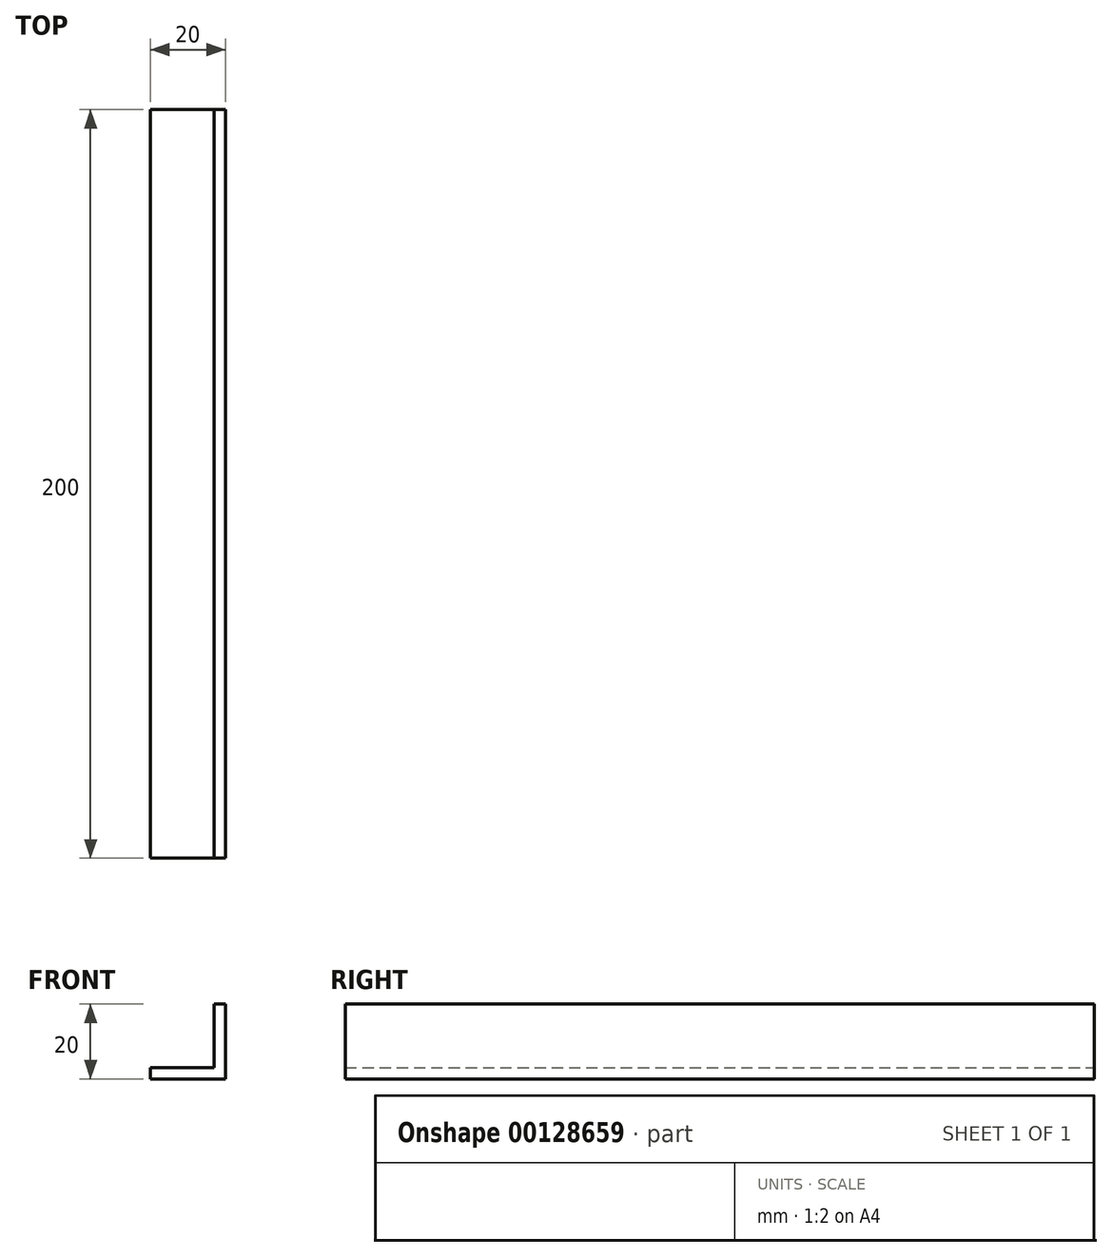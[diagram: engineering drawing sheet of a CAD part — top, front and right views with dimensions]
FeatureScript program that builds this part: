
annotation { "Feature Type Name" : "Feature", "Feature Type Description" : "" }
export const myFeature = defineFeature(function(context is Context, id is Id, definition is map)
    precondition{}
    {
        {
            var Q0;
            Q0=qCreatedBy(makeId("Front.planeOp"),FACE);
            var sketch = newSketch(context, id + "F0", { "sketchPlane" : qUnion([Q0])});
            skLineSegment(sketch, "E0.bottom", {"start": v(-50.63, 3.74) * mm, "end": v(-48.51, 5.86) * mm});
            skLineSegment(sketch, "E0.left", {"start": v(-50.63, 3.74) * mm, "end": v(-36.5, -10.4) * mm});
            skLineSegment(sketch, "E0.right", {"start": v(-48.51, 5.86) * mm, "end": v(-36.5, -6.16) * mm});
            skLineSegment(sketch, "E1.top", {"start": v(-36.5, -6.16) * mm, "end": v(-24.47, 5.86) * mm});
            skLineSegment(sketch, "E1.right", {"start": v(-22.35, 3.74) * mm, "end": v(-24.47, 5.86) * mm});
            skLineSegment(sketch, "E2", {"start": v(-36.5, -10.4) * mm, "end": v(-22.35, 3.74) * mm});
            skCircle(sketch, "E3", {"center": v(-36.48, 8.05) * mm, "radius": 10 * mm});
            skLineSegment(sketch, "E4", {"start": v(62.74, 9.26) * mm, "end": v(264.8, 9.26) * mm});
            skLineSegment(sketch, "E5.0", {"start": v(175.32, -10.74) * mm, "end": v(152.23, -10.74) * mm});
            skLineSegment(sketch, "E5.1", {"start": v(152.23, -10.74) * mm, "end": v(163.77, 9.26) * mm});
            skLineSegment(sketch, "E5.2", {"start": v(163.77, 9.26) * mm, "end": v(175.32, -10.74) * mm});
            skPoint(sketch, "E5.0.midPoint", {"position": v(163.77, -10.74) * mm});
            skLineSegment(sketch, "E6", {"start": v(190.07, -4.08) * mm, "end": v(290.07, -4.08) * mm});
            skCircle(sketch, "E7", {"center": v(290.07, -4.08) * mm, "radius": 5 * mm});
            skCircle(sketch, "E8", {"center": v(163.77, -4.08) * mm, "radius": 6.67 * mm, "construction": true});
            skPoint(sketch, "E8.first.point", {"position": v(158, -0.74) * mm});
            skPoint(sketch, "E8.second.point", {"position": v(169.55, -0.74) * mm});
            skCircle(sketch, "E9", {"center": v(33.81, -4.76) * mm, "radius": 5 * mm});
            skLineSegment(sketch, "E10.MirrorCS", {"start": v(133.81, -4.76) * mm, "end": v(33.81, -4.76) * mm});
            skLineSegment(sketch, "E11", {"start": v(58.5, -219.32) * mm, "end": v(254.7, -219.32) * mm, "construction": true});
            skLineSegment(sketch, "E12", {"start": v(58.5, -203.05) * mm, "end": v(254.7, -164.23) * mm});
            skLineSegment(sketch, "E13", {"start": v(156.6, -183.64) * mm, "end": v(156.6, -183.64) * mm});
            skPoint(sketch, "E13.endSnap0", {"position": v(156.6, -183.64) * mm});
            skLineSegment(sketch, "E14", {"start": v(284.7, -183.64) * mm, "end": v(184.86, -178.05) * mm});
            skLineSegment(sketch, "E15", {"start": v(156.6, -183.64) * mm, "end": v(10.1, -183.64) * mm, "construction": true});
            skLineSegment(sketch, "E16", {"start": v(28.5, -183.64) * mm, "end": v(62.51, -203.24) * mm});
            skLineSegment(sketch, "E17", {"start": v(62.51, -203.24) * mm, "end": v(115.15, -233.57) * mm});
            skLineSegment(sketch, "E18", {"start": v(156.6, -183.64) * mm, "end": v(325.58, -183.64) * mm, "construction": true});
            skSolve(sketch);
        }
        {
            var Q0;
            Q0=makeQuery(id+"F0.imprint","IMPRINT",FACE,{"disambiguationData":[TD([[makeQuery(id+"F0.imprint","IMPRINT",EDGE,{"derivedFrom":sQuery(id+"F0.wireOp",EDGE,"E0.bottom")}),-1.0]])]});
            extrude(context, id + "F1", {"entities" : qUnion([Q0]), "endBound" : BoundingType.SYMMETRIC, "depth" : 200 * mm});
        }
        {
            var Q0;
            Q0=makeQuery(id+"F1.opExtrude","SWEPT_BODY",BODY,{"disambiguationData":[OSD([sQuery(id+"F0.wireOp",EDGE,"E0.bottom"),sQuery(id+"F0.wireOp",EDGE,"E0.left"),sQuery(id+"F0.wireOp",EDGE,"E0.right"),sQuery(id+"F0.wireOp",EDGE,"E1.top"),sQuery(id+"F0.wireOp",EDGE,"E1.right"),sQuery(id+"F0.wireOp",EDGE,"E2")])]});
            var Q1;
            Q1=makeQuery(id+"F1.opExtrude","SWEPT_EDGE",EDGE,{"disambiguationData":[OSD([sQuery(id+"F0.wireOp",EDGE,"E0.left"),sQuery(id+"F0.wireOp",EDGE,"E2")])]});
            transform(context, id + "F2", {"entities" : qUnion([Q0]), "transformType" : TransformType.ROTATION, "transformAxis" : qUnion([Q1]), "angle" : 45 * degree, "oppositeDirection" : true, "makeCopy" : false});
        }
    });
